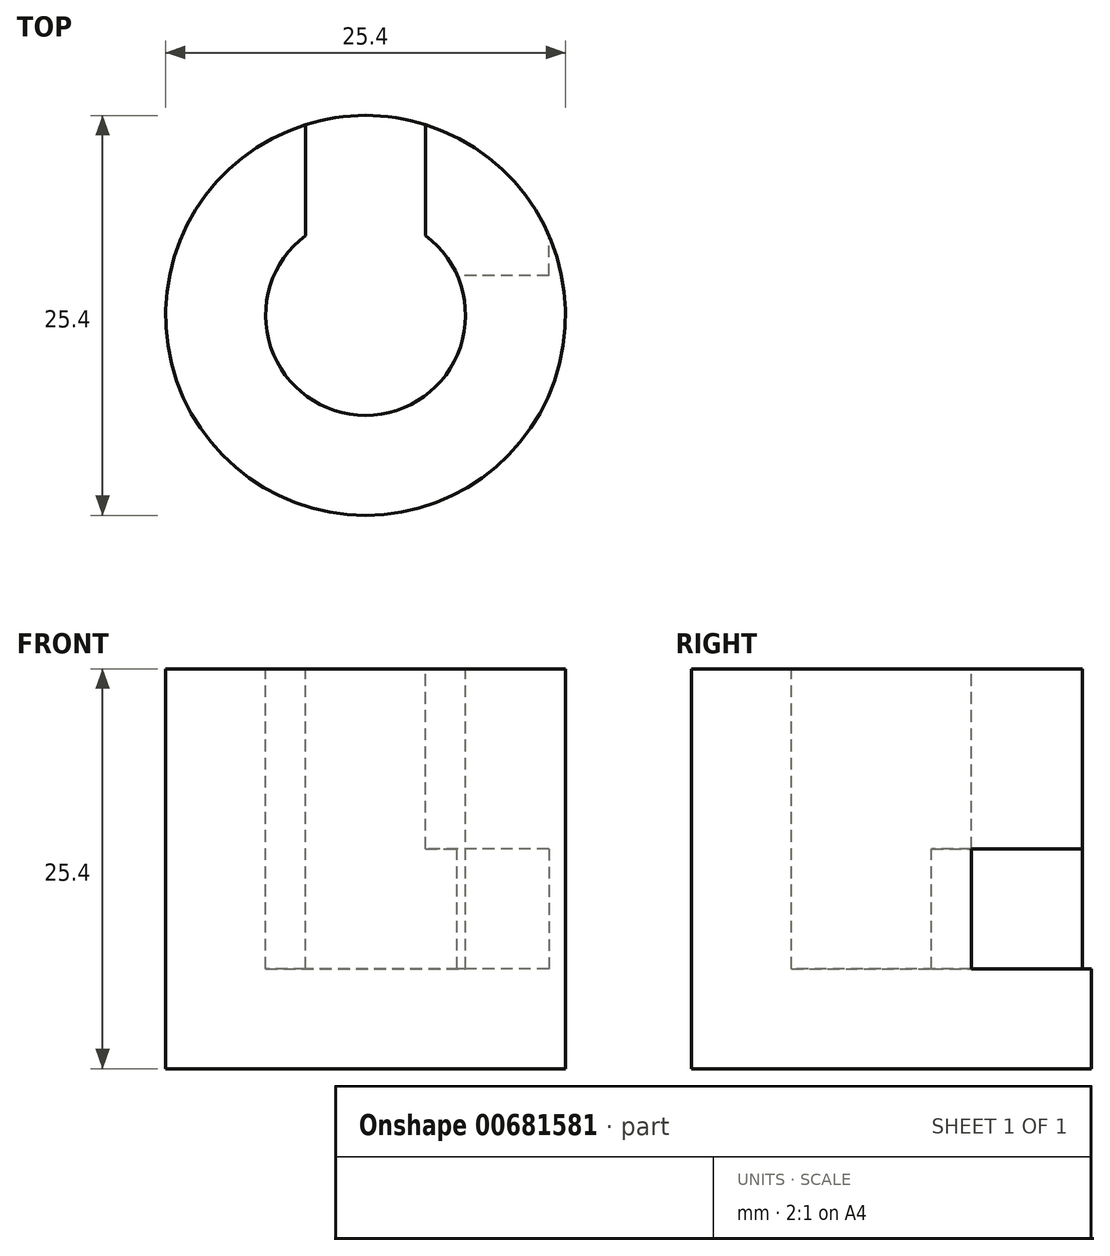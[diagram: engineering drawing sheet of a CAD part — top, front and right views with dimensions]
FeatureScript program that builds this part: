
annotation { "Feature Type Name" : "Feature", "Feature Type Description" : "" }
export const myFeature = defineFeature(function(context is Context, id is Id, definition is map)
    precondition{}
    {
        {
            var Q0;
            Q0=qCreatedBy(makeId("Top.planeOp"),FACE);
            var sketch = newSketch(context, id + "F0", { "sketchPlane" : qUnion([Q0])});
            skCircle(sketch, "E0", {"center": v(0, 0) * mm, "radius": 12.7 * mm});
            skSolve(sketch);
        }
        {
            var Q0;
            Q0=makeQuery(id+"F0.imprint","IMPRINT",FACE,{"disambiguationData":[TD([[makeQuery(id+"F0.imprint","IMPRINT",EDGE,{"derivedFrom":sQuery(id+"F0.wireOp",EDGE,"E0")}),1.0]])]});
            extrude(context, id + "F1", {"entities" : qUnion([Q0]), "depth" : 25.4 * mm, "offsetDistance" : 25.4 * mm});
        }
        {
            var Q0;
            Q0=makeQuery(id+"F1.opExtrude","CAP_FACE",FACE,{"disambiguationData":[OSD([sQuery(id+"F0.wireOp",EDGE,"E0")])],"isStart":false});
            var sketch = newSketch(context, id + "F2", { "sketchPlane" : qUnion([Q0])});
            skCircle(sketch, "E1", {"center": v(0, 0) * mm, "radius": 6.35 * mm});
            skSolve(sketch);
        }
        {
            var Q0;
            Q0=makeQuery(id+"F2.imprint","IMPRINT",FACE,{"disambiguationData":[TD([[makeQuery(id+"F2.imprint","IMPRINT",EDGE,{"derivedFrom":sQuery(id+"F2.wireOp",EDGE,"E1")}),1.0]])]});
            var sketch = newSketch(context, id + "F3", { "sketchPlane" : qUnion([Q0])});
            skLineSegment(sketch, "E2.bottom", {"start": v(0, 0) * mm, "end": v(-3.81, 0) * mm});
            skLineSegment(sketch, "E2.top", {"start": v(0, 12.7) * mm, "end": v(-3.81, 12.7) * mm});
            skLineSegment(sketch, "E2.left", {"start": v(0, 0) * mm, "end": v(0, 12.7) * mm});
            skLineSegment(sketch, "E2.right", {"start": v(-3.81, 0) * mm, "end": v(-3.81, 12.7) * mm});
            skSolve(sketch);
        }
        {
            var Q0;
            Q0=makeQuery(id+"F2.imprint","IMPRINT",FACE,{"disambiguationData":[TD([[makeQuery(id+"F2.imprint","IMPRINT",EDGE,{"derivedFrom":sQuery(id+"F2.wireOp",EDGE,"E1")}),1.0]])]});
            var sketch = newSketch(context, id + "F4", { "sketchPlane" : qUnion([Q0])});
            skLineSegment(sketch, "E3.bottom", {"start": v(0, 0) * mm, "end": v(3.8, 0) * mm});
            skLineSegment(sketch, "E3.top", {"start": v(0, 12.7) * mm, "end": v(3.8, 12.7) * mm});
            skLineSegment(sketch, "E3.left", {"start": v(0, 0) * mm, "end": v(0, 12.7) * mm});
            skLineSegment(sketch, "E3.right", {"start": v(3.8, 0) * mm, "end": v(3.8, 12.7) * mm});
            skSolve(sketch);
        }
        {
            var Q0;
            Q0=makeQuery(id+"F2.imprint","IMPRINT",FACE,{"disambiguationData":[TD([[makeQuery(id+"F2.imprint","IMPRINT",EDGE,{"derivedFrom":sQuery(id+"F2.wireOp",EDGE,"E1")}),1.0]])]});
            var Q1;
            {var subQ0=sQuery(id+"F4.wireOp",EDGE,"E3.top");Q1=makeQuery(id+"F4.imprint","IMPRINT",FACE,{"disambiguationData":[TD([[makeQuery(id+"F4.imprint","IMPRINT",EDGE,{"derivedFrom":subQ0}),-1.0]])]});}
            var Q2;
            {var subQ0=sQuery(id+"F3.wireOp",EDGE,"E2.top");Q2=makeQuery(id+"F3.imprint","IMPRINT",FACE,{"disambiguationData":[TD([[makeQuery(id+"F3.imprint","IMPRINT",EDGE,{"derivedFrom":subQ0}),1.0]])]});}
            extrude(context, id + "F5", {"entities" : qUnion([Q0, Q1, Q2]), "operationType" : NewBodyOperationType.REMOVE, "oppositeDirection" : true, "depth" : 19.05 * mm, "offsetDistance" : 25.4 * mm});
        }
        {
            var Q0;
            Q0=makeQuery(id+"F5.boolean.opBoolean","COPY",FACE,{"derivedFrom":makeQuery(id+"F5.opExtrude","SWEPT_FACE",FACE,{"disambiguationData":[OSD([sQuery(id+"F4.wireOp",EDGE,"E3.right")])]})});
            var sketch = newSketch(context, id + "F6", { "sketchPlane" : qUnion([Q0])});
            skLineSegment(sketch, "E4.bottom", {"start": v(-5.08, 6.35) * mm, "end": v(-12.12, 6.35) * mm});
            skLineSegment(sketch, "E4.top", {"start": v(-5.08, 13.97) * mm, "end": v(-12.12, 13.97) * mm});
            skLineSegment(sketch, "E4.left", {"start": v(-5.08, 6.35) * mm, "end": v(-5.08, 13.97) * mm});
            skLineSegment(sketch, "E4.right", {"start": v(-12.12, 6.35) * mm, "end": v(-12.12, 13.97) * mm});
            skSolve(sketch);
        }
        {
            var Q0;
            Q0=makeQuery(id+"F6.imprint","IMPRINT",FACE,{"disambiguationData":[TD([[makeQuery(id+"F6.imprint","IMPRINT",EDGE,{"derivedFrom":sQuery(id+"F6.wireOp",EDGE,"E4.bottom")}),-1.0]])]});
            extrude(context, id + "F7", {"entities" : qUnion([Q0]), "operationType" : NewBodyOperationType.REMOVE, "oppositeDirection" : true, "depth" : 25.4 * mm, "offsetDistance" : 25.4 * mm});
        }
        {
            var Q0;
            Q0=makeQuery(id+"F7.boolean.opBoolean","COPY",FACE,{"derivedFrom":makeQuery(id+"F7.opExtrude","SWEPT_FACE",FACE,{"disambiguationData":[OSD([sQuery(id+"F6.wireOp",EDGE,"E4.left")])]})});
            extrude(context, id + "F8", {"entities" : qUnion([Q0]), "operationType" : NewBodyOperationType.REMOVE, "oppositeDirection" : true, "depth" : 2.54 * mm, "offsetDistance" : 25.4 * mm});
        }
    });
